# Revit family: Astro_1424xxx_Orb Mirror
name_source: partatom
category: Lighting Fixtures
revit_build: Autodesk Revit 2018 (Build: 20170223_1515(x64)
units: mm (PartAtom-declared; Revit-internal decimal feet)

## family parameters
Always vertical = Yes
Cut with Voids When Loaded = No
Host = Wall
Light Source = No
OmniClass Number = 23.80.70.00
OmniClass Title = Lighting
Part Type = Normal
Room Calculation Point = No
Round Connector Dimension = Use Diameter
Shared = No

## types (2) — shared parameters
ADA compliant = N / A
Dimmable = Yes
Dimming Method = Lamp Dependent
Driver Required = No
Efficacy (lm/w) = Lamp Dependent
Lamp = G9
Light Source Fixed = No
Location / IP Rating = IP44
Main Material = Metal - Steel
Manufacturer = Astro Lighting Ltd
Manufacturer URL - Europe and Rest of World = www.astrolighting.com
Manufacturer URL - North America = us.astrolighting.com
Power (Watts) = 3.5 Watt Max
Product CCT = Lamp Dependent
Product CRI = Lamp Dependent
Product Dimensions (MM) = 434 X 210 X 92
Product Location = Zone 2,3
Product Name = Orb Mirror
Product Weight (KG) = 0.9
URL = www.astrolighting.com
zero-valued in all types: Electrical Class

## per-type parameters (varying)
| type | Main Finish | Product SKU | Product URL |
| Astro Orb Mirror Polished Chrome | Polished Chrome | 1424001 | www.astrolighting.com/1424001 |
| Astro Orb Mirror Matt Black | Matt Black | 1424003 | www.astrolighting.com/1424003 |

## geometry (parser evidence)
native form markers: Sweep x2
no freeform markers — native parametric forms only
